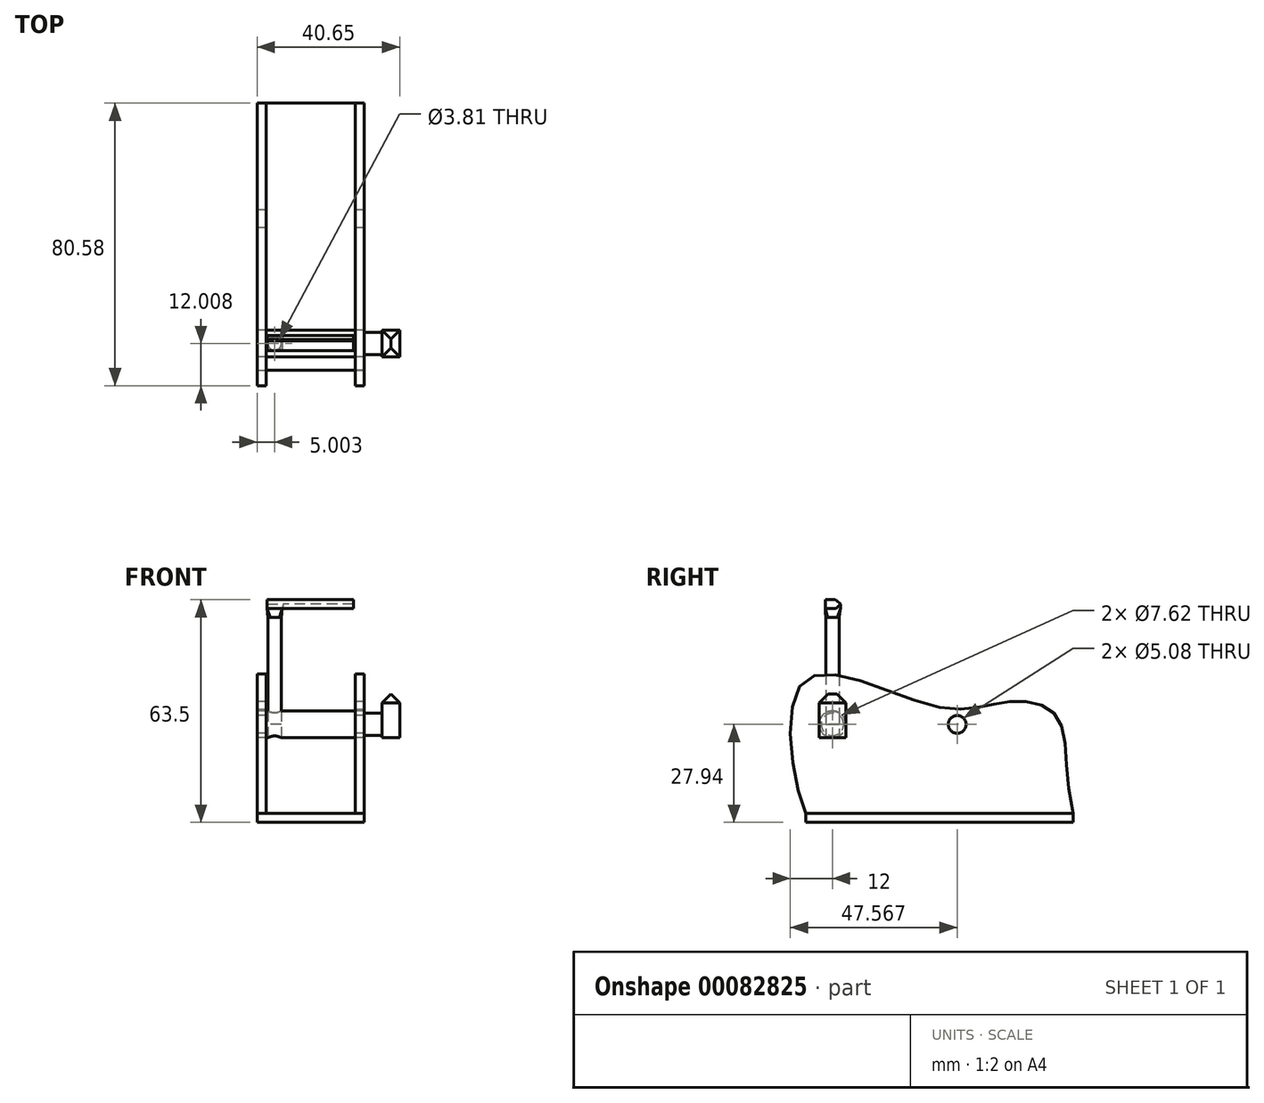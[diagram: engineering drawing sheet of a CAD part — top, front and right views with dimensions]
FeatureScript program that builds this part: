
annotation { "Feature Type Name" : "Feature", "Feature Type Description" : "" }
export const myFeature = defineFeature(function(context is Context, id is Id, definition is map)
    precondition{}
    {
        {
            var Q0;
            Q0=qCreatedBy(makeId("Right.planeOp"),FACE);
            var sketch = newSketch(context, id + "F0", { "sketchPlane" : qUnion([Q0])});
            skLineSegment(sketch, "E0", {"start": v(38.1, 0) * mm, "end": v(0, 0) * mm});
            skLineSegment(sketch, "E1", {"start": v(0, 0) * mm, "end": v(-38.1, 0) * mm});
            skFitSpline(sketch, "E2", {"points": [v(-38.1, 0) * mm, v(-38.1, 38.1) * mm, v(0, 30.26) * mm, v(19.85, 31.93) * mm, v(33.49, 27.63) * mm, v(38.1, 0) * mm], "startDerivative": vector(-50.42, 125.18) * mm, "endDerivative": vector(43.22, -167.1) * mm});
            skSolve(sketch);
        }
        {
            var Q0;
            Q0=makeQuery(id+"F0.imprint","IMPRINT",FACE,{"disambiguationData":[TD([[makeQuery(id+"F0.imprint","IMPRINT",EDGE,{"derivedFrom":sQuery(id+"F0.wireOp",EDGE,"E0")}),-1.0]])]});
            extrude(context, id + "F1", {"entities" : qUnion([Q0]), "depth" : 2.54 * mm});
        }
        {
            var Q0;
            Q0=makeQuery(id+"F1.opExtrude","CAP_FACE",FACE,{"disambiguationData":[OSD([sQuery(id+"F0.wireOp",EDGE,"E0"),sQuery(id+"F0.wireOp",EDGE,"E1"),sQuery(id+"F0.wireOp",EDGE,"E2")])],"isStart":true});
            extrude(context, id + "F2", {"entities" : qUnion([Q0]), "depth" : 2.54 * mm});
        }
        {
            var Q0;
            Q0=makeQuery(id+"F1.opExtrude","SWEPT_BODY",BODY,{"disambiguationData":[OSD([sQuery(id+"F0.wireOp",EDGE,"E0"),sQuery(id+"F0.wireOp",EDGE,"E1"),sQuery(id+"F0.wireOp",EDGE,"E2")])]});
            transform(context, id + "F3", {"entities" : qUnion([Q0]), "transformType" : TransformType.TRANSLATION_3D, "dx" : 12.7 * mm, "dy" : 0 * mm, "dz" : 0 * mm, "makeCopy" : false});
        }
        {
            var Q0;
            Q0=makeQuery(id+"F2.opExtrude","SWEPT_BODY",BODY,{"disambiguationData":[OSD([sQuery(id+"F0.wireOp",EDGE,"E0"),sQuery(id+"F0.wireOp",EDGE,"E1"),sQuery(id+"F0.wireOp",EDGE,"E2")])]});
            transform(context, id + "F4", {"entities" : qUnion([Q0]), "transformType" : TransformType.TRANSLATION_3D, "dx" : -12.7 * mm, "dy" : 0 * mm, "dz" : 0 * mm, "makeCopy" : false});
        }
        {
            var Q0;
            Q0=qCreatedBy(makeId("Top.planeOp"),FACE);
            var sketch = newSketch(context, id + "F5", { "sketchPlane" : qUnion([Q0])});
            skLineSegment(sketch, "E3.bottom", {"start": v(-15.25, -38.12) * mm, "end": v(15.24, -38.12) * mm});
            skLineSegment(sketch, "E3.top", {"start": v(-15.25, 38.1) * mm, "end": v(15.24, 38.1) * mm});
            skLineSegment(sketch, "E3.left", {"start": v(-15.25, -38.12) * mm, "end": v(-15.25, 38.1) * mm});
            skLineSegment(sketch, "E3.right", {"start": v(15.24, -38.12) * mm, "end": v(15.24, 38.1) * mm});
            skSolve(sketch);
        }
        {
            var Q0;
            Q0=makeQuery(id+"F5.imprint","IMPRINT",FACE,{"disambiguationData":[TD([[makeQuery(id+"F5.imprint","IMPRINT",EDGE,{"derivedFrom":sQuery(id+"F5.wireOp",EDGE,"E3.bottom")}),1.0]])]});
            extrude(context, id + "F6", {"entities" : qUnion([Q0]), "oppositeDirection" : true, "depth" : 2.54 * mm});
        }
        {
            var Q0;
            Q0=makeQuery(id+"F1.opExtrude","CAP_FACE",FACE,{"disambiguationData":[OSD([sQuery(id+"F0.wireOp",EDGE,"E0"),sQuery(id+"F0.wireOp",EDGE,"E1"),sQuery(id+"F0.wireOp",EDGE,"E2")])],"isStart":false});
            var sketch = newSketch(context, id + "F7", { "sketchPlane" : qUnion([Q0])});
            skLineSegment(sketch, "E4", {"start": v(-30.48, 0) * mm, "end": v(-30.48, 25.4) * mm});
            skLineSegment(sketch, "E5", {"start": v(-30.48, 25.4) * mm, "end": v(0, 25.4) * mm});
            skCircle(sketch, "E6", {"center": v(-30.48, 25.4) * mm, "radius": 3.81 * mm});
            skSolve(sketch);
        }
        {
            var Q0;
            Q0 = qSketchRegion(id + "F7", true);
            extrude(context, id + "F8", {"entities" : qUnion([Q0]), "operationType" : NewBodyOperationType.REMOVE, "oppositeDirection" : true, "depth" : 32.98 * mm});
        }
        {
            var Q0;
            Q0 = qSketchRegion(id + "F7", true);
            extrude(context, id + "F9", {"entities" : qUnion([Q0]), "depth" : 30.48 * mm});
        }
        {
            var Q0;
            Q0=makeQuery(id+"F9.opExtrude","SWEPT_BODY",BODY,{"disambiguationData":[OSD([sQuery(id+"F7.wireOp",EDGE,"E6")])]});
            transform(context, id + "F10", {"entities" : qUnion([Q0]), "transformType" : TransformType.TRANSLATION_3D, "dx" : -30.48 * mm, "dy" : 0 * mm, "dz" : 0 * mm, "makeCopy" : false});
        }
        {
            var Q0;
            Q0=qCreatedBy(makeId("Front.planeOp"),FACE);
            cPlane(context, id + "F11", {"entities" : qUnion([Q0]), "cplaneType" : CPlaneType.OFFSET, "offset" : 30.48 * mm, "width" : 152.4 * mm, "height" : 152.4 * mm});
        }
        {
            var Q0;
            Q0=makeQuery(id+"F9.opExtrude","CAP_FACE",FACE,{"disambiguationData":[OSD([sQuery(id+"F7.wireOp",EDGE,"E6")])],"isStart":false});
            var sketch = newSketch(context, id + "F12", { "sketchPlane" : qUnion([Q0])});
            skPoint(sketch, "E7", {"position": v(-30.48, 25.4) * mm});
            skSolve(sketch);
        }
        {
            var Q0;
            Q0=makeQuery(id+"F6.opExtrude","CAP_FACE",FACE,{"disambiguationData":[OSD([sQuery(id+"F5.wireOp",EDGE,"E3.bottom"),sQuery(id+"F5.wireOp",EDGE,"E3.top"),sQuery(id+"F5.wireOp",EDGE,"E3.left"),sQuery(id+"F5.wireOp",EDGE,"E3.right")])],"isStart":true});
            var sketch = newSketch(context, id + "F13", { "sketchPlane" : qUnion([Q0])});
            skCircle(sketch, "E8", {"center": v(-10.25, -30.47) * mm, "radius": 1.9 * mm});
            skSolve(sketch);
        }
        {
            var Q0;
            Q0 = qSketchRegion(id + "F13", true);
            extrude(context, id + "F14", {"entities" : qUnion([Q0]), "operationType" : NewBodyOperationType.REMOVE, "depth" : 31.3 * mm});
        }
        {
            var Q0;
            Q0=makeQuery(id+"F6.opExtrude","CAP_FACE",FACE,{"disambiguationData":[OSD([sQuery(id+"F5.wireOp",EDGE,"E3.bottom"),sQuery(id+"F5.wireOp",EDGE,"E3.top"),sQuery(id+"F5.wireOp",EDGE,"E3.left"),sQuery(id+"F5.wireOp",EDGE,"E3.right")])],"isStart":true});
            cPlane(context, id + "F15", {"entities" : qUnion([Q0]), "cplaneType" : CPlaneType.OFFSET, "offset" : 25.4 * mm, "width" : 152.4 * mm, "height" : 152.4 * mm});
        }
        {
            var Q0;
            Q0=qCreatedBy(id+"F15.planeOp",FACE);
            var sketch = newSketch(context, id + "F16", { "sketchPlane" : qUnion([Q0])});
            skCircle(sketch, "E9", {"center": v(-10.25, -30.47) * mm, "radius": 1.9 * mm});
            skPoint(sketch, "E9.first.point", {"position": v(-11.63, -29.16) * mm});
            skPoint(sketch, "E9.second.point", {"position": v(-8.35, -30.63) * mm});
            skPoint(sketch, "E9.third.point", {"position": v(-11.52, -31.9) * mm});
            skSolve(sketch);
        }
        {
            var Q0;
            Q0=makeQuery(id+"F16.imprint","IMPRINT",FACE,{"disambiguationData":[TD([[makeQuery(id+"F16.imprint","IMPRINT",EDGE,{"derivedFrom":sQuery(id+"F16.wireOp",EDGE,"E9")}),1.0]])]});
            extrude(context, id + "F17", {"entities" : qUnion([Q0]), "depth" : 30.48 * mm});
        }
        {
            var Q0;
            Q0=makeQuery(id+"F17.opExtrude","CAP_FACE",FACE,{"disambiguationData":[OSD([sQuery(id+"F16.wireOp",EDGE,"E9")])],"isStart":false});
            cPlane(context, id + "F18", {"entities" : qUnion([Q0]), "cplaneType" : CPlaneType.OFFSET, "offset" : 2.54 * mm, "width" : 152.4 * mm, "height" : 152.4 * mm});
        }
        {
            var Q0;
            Q0=qCreatedBy(id+"F18.planeOp",FACE);
            var sketch = newSketch(context, id + "F19", { "sketchPlane" : qUnion([Q0])});
            skLineSegment(sketch, "E10.bottom", {"start": v(-8.1, -28.2) * mm, "end": v(-12.4, -28.2) * mm});
            skLineSegment(sketch, "E10.top", {"start": v(-8.1, -32.5) * mm, "end": v(-12.4, -32.5) * mm});
            skLineSegment(sketch, "E10.left", {"start": v(-8.1, -28.2) * mm, "end": v(-8.1, -32.5) * mm});
            skLineSegment(sketch, "E10.right", {"start": v(-12.4, -28.2) * mm, "end": v(-12.4, -32.5) * mm});
            skPoint(sketch, "E10.middle", {"position": v(-10.25, -30.35) * mm});
            skSolve(sketch);
        }
        {
            var Q0;
            Q0=makeQuery(id+"F19.imprint","IMPRINT",FACE,{"disambiguationData":[TD([[makeQuery(id+"F19.imprint","IMPRINT",EDGE,{"derivedFrom":sQuery(id+"F19.wireOp",EDGE,"E10.bottom")}),1.0]])]});
            var Q1;
            Q1=makeQuery(id+"F17.opExtrude","CAP_FACE",FACE,{"disambiguationData":[OSD([sQuery(id+"F16.wireOp",EDGE,"E9")])],"isStart":false});
            var Q2;
            Q2=makeQuery(id+"F17.opExtrude","CAP_FACE",FACE,{"disambiguationData":[OSD([sQuery(id+"F16.wireOp",EDGE,"E9")])],"isStart":false});
            var Q3;
            Q3=makeQuery(id+"F19.imprint","IMPRINT",FACE,{"disambiguationData":[TD([[makeQuery(id+"F19.imprint","IMPRINT",EDGE,{"derivedFrom":sQuery(id+"F19.wireOp",EDGE,"E10.bottom")}),1.0]])]});
            loft(context, id + "F20", {"sheetProfilesArray" : [{ "sheetProfileEntities" : qUnion([Q0]) }, { "sheetProfileEntities" : qUnion([Q1]) }], "wireProfilesArray" : [{ "wireProfileEntities" : qUnion([Q2]) }, { "wireProfileEntities" : qUnion([Q3]) }]});
        }
        {
            var Q0;
            Q0=makeQuery(id+"F20.opLoft","CAP_FACE",FACE,{"disambiguationData":[OSD([makeQuery(id+"F19.imprint","IMPRINT",FACE,{"disambiguationData":[TD([[makeQuery(id+"F19.imprint","IMPRINT",EDGE,{"derivedFrom":sQuery(id+"F19.wireOp",EDGE,"E10.bottom")}),1.0]])]})])],"isStart":true});
            extrude(context, id + "F21", {"entities" : qUnion([Q0]), "operationType" : NewBodyOperationType.ADD, "depth" : 2.54 * mm});
        }
        {
            var Q0;
            Q0=makeQuery(id+"F21.opExtrude","SWEPT_FACE",FACE,{"disambiguationData":[OSD([sQuery(id+"F19.wireOp",EDGE,"E10.bottom"),sQuery(id+"F19.wireOp",EDGE,"E10.top"),sQuery(id+"F19.wireOp",EDGE,"E10.left")])]});
            extrude(context, id + "F22", {"entities" : qUnion([Q0]), "operationType" : NewBodyOperationType.ADD, "depth" : 20.32 * mm});
        }
        {
            var Q0;
            {var subQ0=sQuery(id+"F19.wireOp",EDGE,"E10.left");var subQ1=sQuery(id+"F19.wireOp",EDGE,"E10.bottom");Q0=makeQuery(id+"F22.opExtrude","SWEPT_EDGE",EDGE,{"disambiguationData":[OSD([subQ1,subQ0]),TDD([makeQuery(id+"F21.opExtrude","CAP_VERTEX",VERTEX,{"disambiguationData":[OSD([subQ1,subQ0])],"isStart":false})])]});}
            var Q1;
            {var subQ0=sQuery(id+"F19.wireOp",EDGE,"E10.left");var subQ1=sQuery(id+"F19.wireOp",EDGE,"E10.bottom");Q1=makeQuery(id+"F22.opExtrude","SWEPT_EDGE",EDGE,{"disambiguationData":[OSD([subQ1,subQ0]),TDD([makeQuery(id+"F21.boolean.opBoolean","MERGE",VERTEX,{"derivedFrom":[makeQuery(id+"F20.opLoft","MID_CAP_VERTEX",VERTEX,{"disambiguationData":[OSD([subQ1,subQ0])],"capPos":0.0}),makeQuery(id+"F21.opExtrude","CAP_VERTEX",VERTEX,{"disambiguationData":[OSD([subQ1,subQ0])],"isStart":true})]})])]});}
            chamfer(context, id + "F23", {"entities" : qUnion([Q0, Q1]), "width" : 1.27 * mm, "tangentPropagation" : true});
        }
        {
            var Q0;
            {var subQ0=sQuery(id+"F19.wireOp",EDGE,"E10.left");var subQ1=sQuery(id+"F19.wireOp",EDGE,"E10.top");var subQ2=sQuery(id+"F19.wireOp",EDGE,"E10.bottom");var subQ3=sQuery(id+"F19.wireOp",EDGE,"E10.right");Q0=makeQuery(id+"F23.opChamfer","BLEND_EDGE",EDGE,{"blendedFrom":[makeQuery(id+"F21.opExtrude","CAP_EDGE",EDGE,{"disambiguationData":[OSD([subQ2,subQ0,subQ3])],"isStart":false}),makeQuery(id+"F22.boolean.opBoolean","MERGE",FACE,{"derivedFrom":[makeQuery(id+"F21.opExtrude","CAP_FACE",FACE,{"disambiguationData":[OSD([makeQuery(id+"F19.imprint","IMPRINT",FACE,{"disambiguationData":[TD([[makeQuery(id+"F19.imprint","IMPRINT",EDGE,{"derivedFrom":subQ2}),1.0]])]})])],"isStart":false}),makeQuery(id+"F22.opExtrude","SWEPT_FACE",FACE,{"disambiguationData":[OSD([subQ2,subQ1,subQ0]),TDD([makeQuery(id+"F21.opExtrude","CAP_EDGE",EDGE,{"disambiguationData":[OSD([subQ2,subQ1,subQ0])],"isStart":false})])]})]})],"blendedInto":[makeQuery(id+"F22.boolean.opBoolean","MERGE",FACE,{"derivedFrom":[makeQuery(id+"F21.opExtrude","CAP_FACE",FACE,{"disambiguationData":[OSD([makeQuery(id+"F19.imprint","IMPRINT",FACE,{"disambiguationData":[TD([[makeQuery(id+"F19.imprint","IMPRINT",EDGE,{"derivedFrom":subQ2}),1.0]])]})])],"isStart":false}),makeQuery(id+"F22.opExtrude","SWEPT_FACE",FACE,{"disambiguationData":[OSD([subQ2,subQ1,subQ0]),TDD([makeQuery(id+"F21.opExtrude","CAP_EDGE",EDGE,{"disambiguationData":[OSD([subQ2,subQ1,subQ0])],"isStart":false})])]})]})]});}
            var Q1;
            {var subQ0=sQuery(id+"F19.wireOp",EDGE,"E10.left");var subQ1=sQuery(id+"F19.wireOp",EDGE,"E10.top");var subQ2=sQuery(id+"F19.wireOp",EDGE,"E10.bottom");Q1=makeQuery(id+"F23.opChamfer","BLEND_EDGE",EDGE,{"blendedFrom":[makeQuery(id+"F22.opExtrude","SWEPT_EDGE",EDGE,{"disambiguationData":[OSD([subQ2,subQ0]),TDD([makeQuery(id+"F21.boolean.opBoolean","MERGE",VERTEX,{"derivedFrom":[makeQuery(id+"F20.opLoft","MID_CAP_VERTEX",VERTEX,{"disambiguationData":[OSD([subQ2,subQ0])],"capPos":0.0}),makeQuery(id+"F21.opExtrude","CAP_VERTEX",VERTEX,{"disambiguationData":[OSD([subQ2,subQ0])],"isStart":true})]})])]}),makeQuery(id+"F22.opExtrude","SWEPT_FACE",FACE,{"disambiguationData":[OSD([subQ2,subQ1,subQ0]),TDD([makeQuery(id+"F21.boolean.opBoolean","MERGE",EDGE,{"derivedFrom":[makeQuery(id+"F20.opLoft","MID_CAP_EDGE",EDGE,{"disambiguationData":[OSD([subQ2,subQ1,subQ0])],"capPos":0.0}),makeQuery(id+"F21.opExtrude","CAP_EDGE",EDGE,{"disambiguationData":[OSD([subQ2,subQ1,subQ0])],"isStart":true})]})])]})],"blendedInto":[makeQuery(id+"F22.opExtrude","SWEPT_FACE",FACE,{"disambiguationData":[OSD([subQ2,subQ1,subQ0]),TDD([makeQuery(id+"F21.boolean.opBoolean","MERGE",EDGE,{"derivedFrom":[makeQuery(id+"F20.opLoft","MID_CAP_EDGE",EDGE,{"disambiguationData":[OSD([subQ2,subQ1,subQ0])],"capPos":0.0}),makeQuery(id+"F21.opExtrude","CAP_EDGE",EDGE,{"disambiguationData":[OSD([subQ2,subQ1,subQ0])],"isStart":true})]})])]})]});}
            chamfer(context, id + "F24", {"entities" : qUnion([Q0, Q1]), "width" : 0.64 * mm, "tangentPropagation" : true});
        }
        {
            var Q0;
            Q0=makeQuery(id+"F12.imprint","IMPRINT",FACE,{"disambiguationData":[TD([[makeQuery(id+"F12.imprint","IMPRINT",EDGE,{"derivedFrom":makeQuery(id+"F9.opExtrude","CAP_EDGE",EDGE,{"disambiguationData":[OSD([sQuery(id+"F7.wireOp",EDGE,"E6")])],"isStart":false})}),1.0]])]});
            var sketch = newSketch(context, id + "F25", { "sketchPlane" : qUnion([Q0])});
            skCircle(sketch, "E11", {"center": v(-30.46, 25.4) * mm, "radius": 3.2 * mm});
            skSolve(sketch);
        }
        {
            var Q0;
            Q0 = qSketchRegion(id + "F25", true);
            extrude(context, id + "F26", {"entities" : qUnion([Q0]), "operationType" : NewBodyOperationType.ADD, "depth" : 5.08 * mm});
        }
        {
            var Q0;
            Q0=makeQuery(id+"F26.opExtrude","CAP_FACE",FACE,{"disambiguationData":[OSD([sQuery(id+"F25.wireOp",EDGE,"E11")])],"isStart":false});
            var sketch = newSketch(context, id + "F27", { "sketchPlane" : qUnion([Q0])});
            skLineSegment(sketch, "E12.bottom", {"start": v(-34.27, 21.62) * mm, "end": v(-26.66, 21.62) * mm});
            skLineSegment(sketch, "E12.top", {"start": v(-34.27, 34.12) * mm, "end": v(-26.66, 34.12) * mm});
            skLineSegment(sketch, "E12.left", {"start": v(-34.27, 21.62) * mm, "end": v(-34.27, 34.12) * mm});
            skLineSegment(sketch, "E12.right", {"start": v(-26.66, 21.62) * mm, "end": v(-26.66, 34.12) * mm});
            skSolve(sketch);
        }
        {
            var Q0;
            Q0 = qSketchRegion(id + "F27", true);
            extrude(context, id + "F28", {"entities" : qUnion([Q0]), "operationType" : NewBodyOperationType.ADD, "depth" : 5.08 * mm});
        }
        {
            var Q0;
            Q0=makeQuery(id+"F28.opExtrude","SWEPT_EDGE",EDGE,{"disambiguationData":[OSD([sQuery(id+"F27.wireOp",EDGE,"E12.top"),sQuery(id+"F27.wireOp",EDGE,"E12.left")])]});
            var Q1;
            Q1=makeQuery(id+"F28.opExtrude","CAP_EDGE",EDGE,{"disambiguationData":[OSD([sQuery(id+"F27.wireOp",EDGE,"E12.top")])],"isStart":false});
            var Q2;
            Q2=makeQuery(id+"F28.opExtrude","CAP_EDGE",EDGE,{"disambiguationData":[OSD([sQuery(id+"F27.wireOp",EDGE,"E12.top")])],"isStart":true});
            var Q3;
            Q3=makeQuery(id+"F28.opExtrude","SWEPT_EDGE",EDGE,{"disambiguationData":[OSD([sQuery(id+"F27.wireOp",EDGE,"E12.top"),sQuery(id+"F27.wireOp",EDGE,"E12.right")])]});
            chamfer(context, id + "F29", {"entities" : qUnion([Q0, Q1, Q2, Q3]), "width" : 2.54 * mm, "tangentPropagation" : true});
        }
        {
            var Q0;
            Q0=makeQuery(id+"F2.opExtrude","CAP_FACE",FACE,{"disambiguationData":[OSD([sQuery(id+"F0.wireOp",EDGE,"E0"),sQuery(id+"F0.wireOp",EDGE,"E1"),sQuery(id+"F0.wireOp",EDGE,"E2")])],"isStart":false});
            var sketch = newSketch(context, id + "F30", { "sketchPlane" : qUnion([Q0])});
            skCircle(sketch, "E13", {"center": v(-5.09, 25.4) * mm, "radius": 2.54 * mm});
            skSolve(sketch);
        }
        {
            var Q0;
            Q0 = qSketchRegion(id + "F30", true);
            extrude(context, id + "F31", {"entities" : qUnion([Q0]), "operationType" : NewBodyOperationType.REMOVE, "oppositeDirection" : true, "depth" : 127 * mm});
        }
    });
